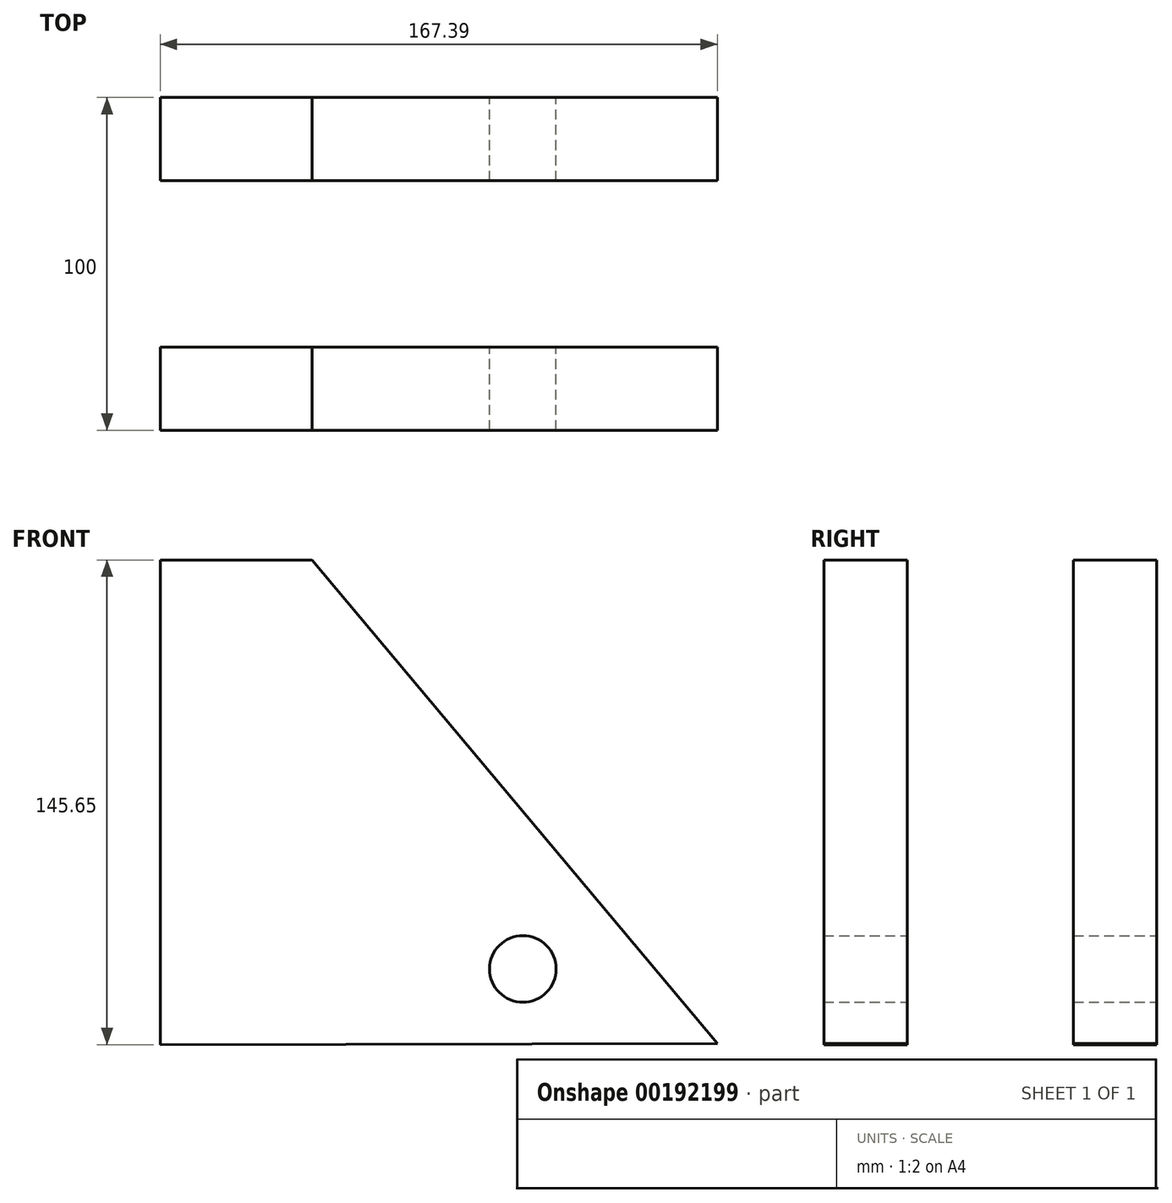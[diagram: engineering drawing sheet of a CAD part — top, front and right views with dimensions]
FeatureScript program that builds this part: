
annotation { "Feature Type Name" : "Feature", "Feature Type Description" : "" }
export const myFeature = defineFeature(function(context is Context, id is Id, definition is map)
    precondition{}
    {
        {
            var Q0;
            Q0=qCreatedBy(makeId("Front.planeOp"),FACE);
            var sketch = newSketch(context, id + "F0", { "sketchPlane" : qUnion([Q0])});
            skLineSegment(sketch, "E0.left", {"start": v(-53.66, -100) * mm, "end": v(-53.66, 45.65) * mm});
            skPoint(sketch, "E0.middle", {"position": v(-73.66, 0) * mm});
            skLineSegment(sketch, "E1", {"start": v(-8.1, 45.65) * mm, "end": v(113.73, -99.7) * mm});
            skLineSegment(sketch, "E2", {"start": v(113.73, -99.7) * mm, "end": v(-53.66, -100) * mm});
            skLineSegment(sketch, "E3", {"start": v(-8.1, 45.65) * mm, "end": v(-53.66, 45.65) * mm});
            skCircle(sketch, "E4", {"center": v(55.29, -77.26) * mm, "radius": 10 * mm});
            skSolve(sketch);
        }
        {
            var Q0;
            Q0 = qSketchRegion(id + "F0", true);
            extrude(context, id + "F1", {"entities" : qUnion([Q0]), "depth" : 100 * mm, "symmetric" : true});
        }
        {
            var Q0;
            Q0 = qSketchRegion(id + "F0", true);
            extrude(context, id + "F2", {"entities" : qUnion([Q0]), "operationType" : NewBodyOperationType.ADD, "oppositeDirection" : true, "depth" : 90 * mm, "symmetric" : true});
        }
        {
            var Q0;
            Q0=qCreatedBy(makeId("Top.planeOp"),FACE);
            var sketch = newSketch(context, id + "F3", { "sketchPlane" : qUnion([Q0])});
            skLineSegment(sketch, "E5.bottom", {"start": v(116.54, -25) * mm, "end": v(-83.46, -25) * mm});
            skLineSegment(sketch, "E5.top", {"start": v(116.54, 25) * mm, "end": v(-83.46, 25) * mm});
            skLineSegment(sketch, "E5.left", {"start": v(116.54, -25) * mm, "end": v(116.54, 25) * mm});
            skLineSegment(sketch, "E5.right", {"start": v(-83.46, -25) * mm, "end": v(-83.46, 25) * mm});
            skPoint(sketch, "E5.middle", {"position": v(16.54, 0) * mm});
            skSolve(sketch);
        }
        {
            var Q0;
            Q0=makeQuery(id+"F3.imprint","IMPRINT",FACE,{"disambiguationData":[TD([[makeQuery(id+"F3.imprint","IMPRINT",EDGE,{"derivedFrom":sQuery(id+"F3.wireOp",EDGE,"E5.bottom")}),-1.0]])]});
            extrude(context, id + "F4", {"entities" : qUnion([Q0]), "operationType" : NewBodyOperationType.REMOVE, "oppositeDirection" : true, "depth" : 400 * mm, "symmetric" : true});
        }
    });
